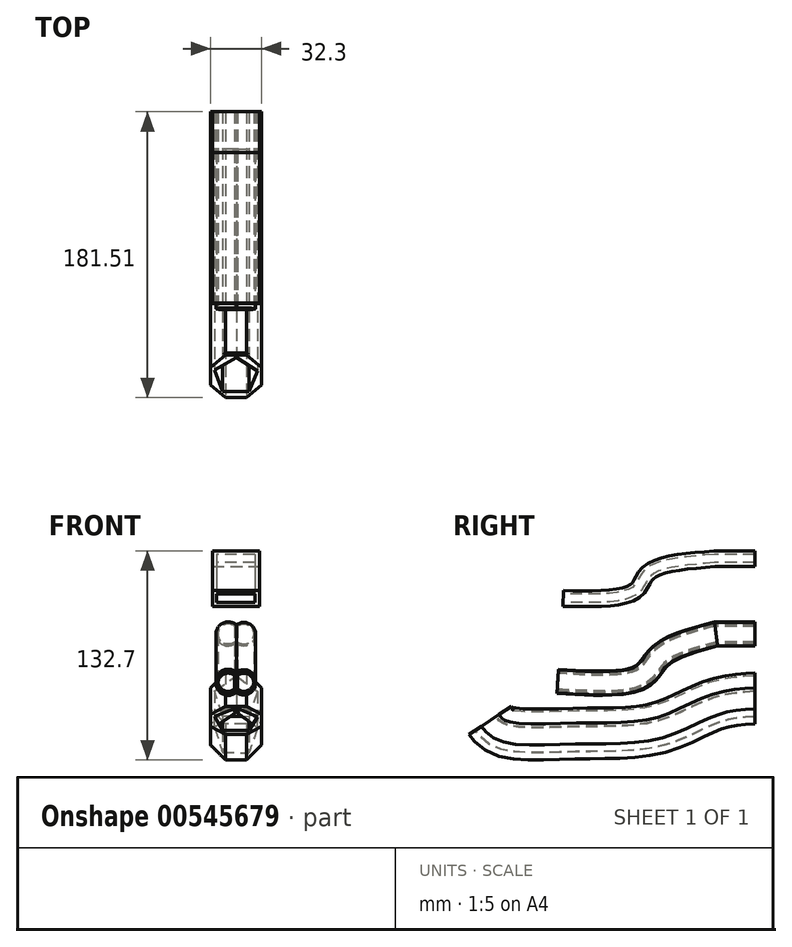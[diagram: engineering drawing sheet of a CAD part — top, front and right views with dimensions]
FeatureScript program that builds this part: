
annotation { "Feature Type Name" : "Feature", "Feature Type Description" : "" }
export const myFeature = defineFeature(function(context is Context, id is Id, definition is map)
    precondition{}
    {
        {
            var Q0;
            Q0=qCreatedBy(makeId("Front.planeOp"),FACE);
            var sketch = newSketch(context, id + "F0", { "sketchPlane" : qUnion([Q0])});
            skCircle(sketch, "E0", {"center": v(5, 0) * mm, "radius": 7.4 * mm});
            skCircle(sketch, "E1", {"center": v(0, 0) * mm, "radius": 5 * mm});
            skCircle(sketch, "E2", {"center": v(-5, 0) * mm, "radius": 7.7 * mm});
            skCircle(sketch, "E3", {"center": v(-5, 0) * mm, "radius": 6.42 * mm});
            skCircle(sketch, "E4", {"center": v(5, 0) * mm, "radius": 6.4 * mm});
            skSolve(sketch);
        }
        {
            var Q0;
            Q0=qCreatedBy(makeId("Right.planeOp"),FACE);
            var sketch = newSketch(context, id + "F1", { "sketchPlane" : qUnion([Q0])});
            skLineSegment(sketch, "E5", {"start": v(0, 0) * mm, "end": v(-24.64, 0) * mm});
            skFitSpline(sketch, "E6", {"points": [v(-24.64, 0) * mm, v(-60.05, -13.88) * mm, v(-72.23, -27.2) * mm, v(-125.2, -30.03) * mm], "startDerivative": vector(-121.68, -32.27) * mm, "endDerivative": vector(-157.7, 10.1) * mm});
            skSolve(sketch);
        }
        {
            var Q0;
            Q0 = qSketchRegion(id + "F0", true);
            var Q1;
            Q1 = qConstructionFilter(qBodyType(qCreatedBy(id + "F1" ,EDGE), BodyType.WIRE), ConstructionObject.NO);
            sweep(context, id + "F2", {"profiles" : qUnion([Q0]), "path" : qUnion([Q1])});
        }
        {
            var Q0;
            Q0=qCreatedBy(makeId("Front.planeOp"),FACE);
            var sketch = newSketch(context, id + "F3", { "sketchPlane" : qUnion([Q0])});
            skLineSegment(sketch, "E7.bottom", {"start": v(-15, 52.77) * mm, "end": v(15, 52.77) * mm});
            skLineSegment(sketch, "E7.top", {"start": v(-15, 42.77) * mm, "end": v(15, 42.77) * mm});
            skLineSegment(sketch, "E7.left", {"start": v(-15, 52.77) * mm, "end": v(-15, 42.77) * mm});
            skLineSegment(sketch, "E7.right", {"start": v(15, 52.77) * mm, "end": v(15, 42.77) * mm});
            skLineSegment(sketch, "E8.bottom", {"start": v(11.95, 50.7) * mm, "end": v(-12.4, 50.7) * mm});
            skLineSegment(sketch, "E8.top", {"start": v(11.95, 45.32) * mm, "end": v(-12.4, 45.32) * mm});
            skLineSegment(sketch, "E8.left", {"start": v(11.95, 50.7) * mm, "end": v(11.95, 45.32) * mm});
            skLineSegment(sketch, "E8.right", {"start": v(-12.4, 50.7) * mm, "end": v(-12.4, 45.32) * mm});
            skSolve(sketch);
        }
        {
            var Q0;
            Q0=qCreatedBy(makeId("Right.planeOp"),FACE);
            var sketch = newSketch(context, id + "F4", { "sketchPlane" : qUnion([Q0])});
            skLineSegment(sketch, "E9", {"start": v(0, 48.16) * mm, "end": v(-25.63, 48.16) * mm});
            skFitSpline(sketch, "E10", {"points": [v(-25.63, 48.16) * mm, v(-67.66, 39.45) * mm, v(-76.16, 27.83) * mm, v(-121.77, 23.02) * mm], "startDerivative": vector(-137.73, -10.68) * mm, "endDerivative": vector(-145.11, 2.96) * mm});
            skSolve(sketch);
        }
        {
            var Q0;
            Q0=makeQuery(id+"F3.imprint","IMPRINT",FACE,{"disambiguationData":[TD([[makeQuery(id+"F3.imprint","IMPRINT",EDGE,{"derivedFrom":sQuery(id+"F3.wireOp",EDGE,"E7.bottom")}),-1.0]])]});
            var Q1;
            Q1=sQuery(id+"F4.wireOp",EDGE,"E9");
            var Q2;
            Q2=sQuery(id+"F4.wireOp",EDGE,"E10");
            sweep(context, id + "F5", {"profiles" : qUnion([Q0]), "path" : qUnion([Q1, Q2])});
        }
        {
            var Q0;
            Q0=qCreatedBy(makeId("Front.planeOp"),FACE);
            var sketch = newSketch(context, id + "F6", { "sketchPlane" : qUnion([Q0])});
            skCircle(sketch, "E11.cCircle", {"center": v(0, -40.8) * mm, "radius": 16.15 * mm, "construction": true});
            skLineSegment(sketch, "E11.0", {"start": v(-16.15, -47.48) * mm, "end": v(-16.15, -34.1) * mm});
            skLineSegment(sketch, "E11.1", {"start": v(-16.15, -34.1) * mm, "end": v(-6.69, -24.64) * mm});
            skLineSegment(sketch, "E11.2", {"start": v(-6.69, -24.64) * mm, "end": v(6.69, -24.64) * mm});
            skLineSegment(sketch, "E11.3", {"start": v(6.69, -24.64) * mm, "end": v(16.15, -34.1) * mm});
            skLineSegment(sketch, "E11.4", {"start": v(16.15, -34.1) * mm, "end": v(16.15, -47.48) * mm});
            skLineSegment(sketch, "E11.5", {"start": v(16.15, -47.48) * mm, "end": v(6.69, -56.94) * mm});
            skLineSegment(sketch, "E11.6", {"start": v(6.69, -56.94) * mm, "end": v(-6.69, -56.94) * mm});
            skLineSegment(sketch, "E11.7", {"start": v(-6.69, -56.94) * mm, "end": v(-16.15, -47.48) * mm});
            skPoint(sketch, "E11.0.midPoint", {"position": v(-16.15, -40.8) * mm});
            skCircle(sketch, "E12.cCircle", {"center": v(0, -40.8) * mm, "radius": 11.56 * mm, "construction": true});
            skLineSegment(sketch, "E12.0", {"start": v(-8.58, -52.22) * mm, "end": v(-13.52, -36.16) * mm});
            skLineSegment(sketch, "E12.1", {"start": v(-13.52, -36.16) * mm, "end": v(0.22, -26.5) * mm});
            skLineSegment(sketch, "E12.2", {"start": v(0.22, -26.5) * mm, "end": v(13.66, -36.59) * mm});
            skLineSegment(sketch, "E12.3", {"start": v(13.66, -36.59) * mm, "end": v(8.22, -52.48) * mm});
            skLineSegment(sketch, "E12.4", {"start": v(8.22, -52.48) * mm, "end": v(-8.58, -52.22) * mm});
            skPoint(sketch, "E12.0.midPoint", {"position": v(-11.05, -44.2) * mm});
            skSolve(sketch);
        }
        {
            var Q0;
            Q0=qCreatedBy(makeId("Right.planeOp"),FACE);
            var sketch = newSketch(context, id + "F7", { "sketchPlane" : qUnion([Q0])});
            skFitSpline(sketch, "E13", {"points": [v(0, -40.5) * mm, v(-26.2, -44.76) * mm, v(-60.76, -59.2) * mm, v(-111.46, -62.89) * mm, v(-159.34, -61.47) * mm, v(-167.84, -54.67) * mm], "startDerivative": vector(-143.56, -9.65) * mm, "endDerivative": vector(-52.46, 68.3) * mm});
            skSolve(sketch);
        }
        {
            var Q0;
            Q0=makeQuery(id+"F6.imprint","IMPRINT",FACE,{"disambiguationData":[TD([[makeQuery(id+"F6.imprint","IMPRINT",EDGE,{"derivedFrom":sQuery(id+"F6.wireOp",EDGE,"E11.0")}),-1.0]])]});
            var Q1;
            Q1=sQuery(id+"F7.wireOp",EDGE,"E13");
            sweep(context, id + "F8", {"profiles" : qUnion([Q0]), "path" : qUnion([Q1])});
        }
    });
